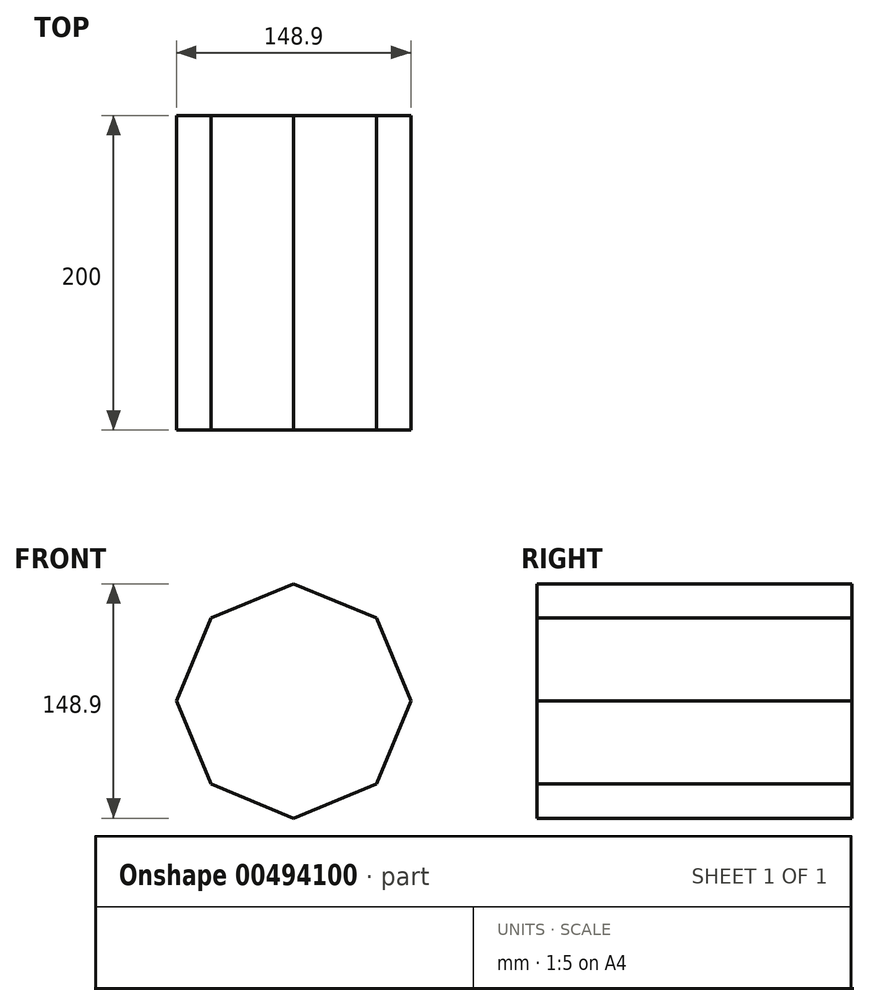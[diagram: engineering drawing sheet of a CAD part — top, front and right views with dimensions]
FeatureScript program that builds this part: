
annotation { "Feature Type Name" : "Feature", "Feature Type Description" : "" }
export const myFeature = defineFeature(function(context is Context, id is Id, definition is map)
    precondition{}
    {
        {
            var Q0;
            Q0=qCreatedBy(makeId("Front.planeOp"),FACE);
            var sketch = newSketch(context, id + "F0", { "sketchPlane" : qUnion([Q0])});
            skCircle(sketch, "E0.cCircle", {"center": v(0, 0) * mm, "radius": 74.45 * mm, "construction": true});
            skLineSegment(sketch, "E0.0", {"start": v(0, 74.45) * mm, "end": v(52.64, 52.64) * mm});
            skLineSegment(sketch, "E0.1", {"start": v(52.64, 52.64) * mm, "end": v(74.45, 0) * mm});
            skLineSegment(sketch, "E0.2", {"start": v(74.45, 0) * mm, "end": v(52.64, -52.64) * mm});
            skLineSegment(sketch, "E0.3", {"start": v(52.64, -52.64) * mm, "end": v(0, -74.45) * mm});
            skLineSegment(sketch, "E0.4", {"start": v(0, -74.45) * mm, "end": v(-52.64, -52.64) * mm});
            skLineSegment(sketch, "E0.5", {"start": v(-52.64, -52.64) * mm, "end": v(-74.45, 0) * mm});
            skLineSegment(sketch, "E0.6", {"start": v(-74.45, 0) * mm, "end": v(-52.64, 52.64) * mm});
            skLineSegment(sketch, "E0.7", {"start": v(-52.64, 52.64) * mm, "end": v(0, 74.45) * mm});
            skSolve(sketch);
        }
        {
            var Q0;
            Q0 = qSketchRegion(id + "F0", true);
            extrude(context, id + "F1", {"entities" : qUnion([Q0]), "depth" : 200 * mm});
        }
    });
